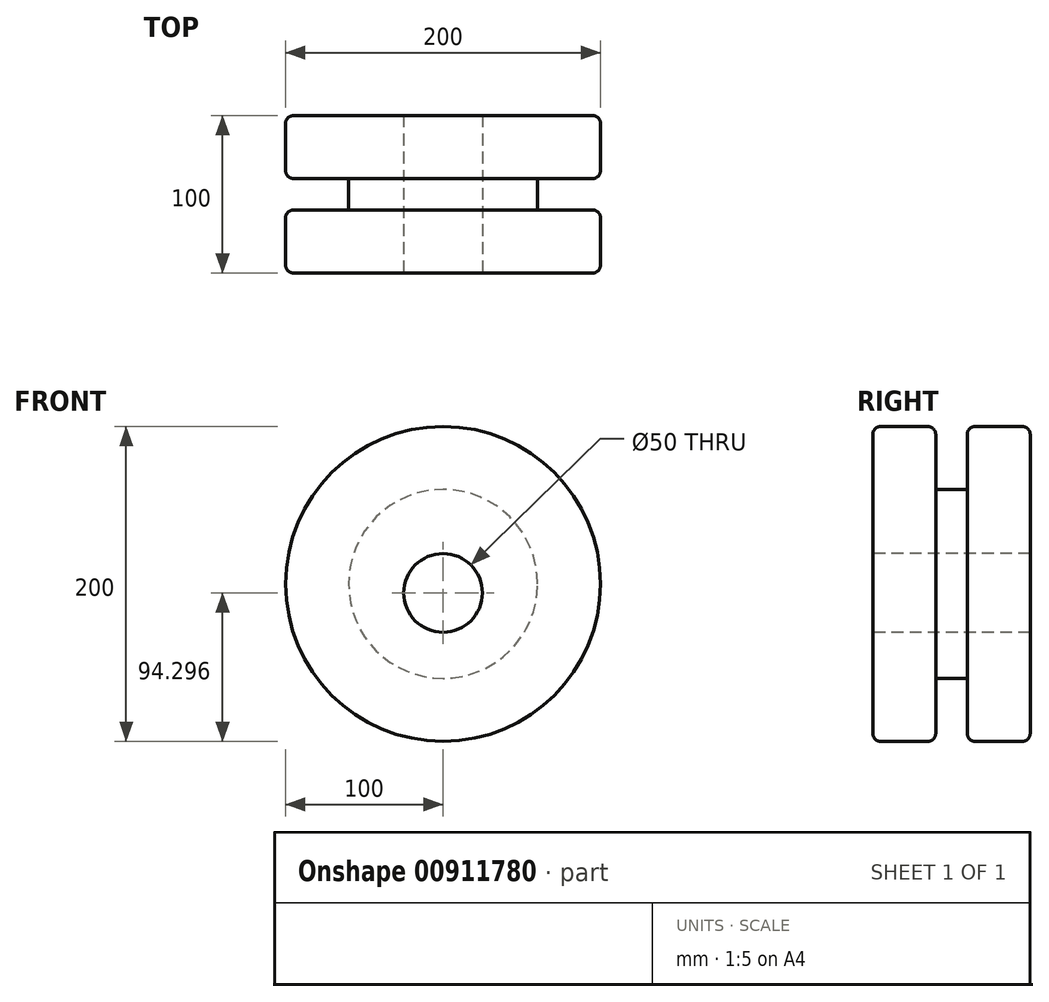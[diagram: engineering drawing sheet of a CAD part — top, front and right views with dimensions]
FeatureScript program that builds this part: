
annotation { "Feature Type Name" : "Feature", "Feature Type Description" : "" }
export const myFeature = defineFeature(function(context is Context, id is Id, definition is map)
    precondition{}
    {
        {
            var Q0;
            Q0=qCreatedBy(makeId("Front.planeOp"),FACE);
            var sketch = newSketch(context, id + "F0", { "sketchPlane" : qUnion([Q0])});
            skCircle(sketch, "E0", {"center": v(0, 0) * mm, "radius": 100 * mm});
            skSolve(sketch);
        }
        {
            var Q0;
            Q0=qSketchRegion(id+"F0",true);
            extrude(context, id + "F1", {"entities" : qUnion([Q0]), "depth" : 40 * mm, "offsetDistance" : 25 * mm});
        }
        {
            var Q0;
            Q0=makeQuery(id+"F1.opExtrude","CAP_FACE",FACE,{"disambiguationData":[OSD([sQuery(id+"F0.wireOp",EDGE,"E0")])],"isStart":false});
            var sketch = newSketch(context, id + "F2", { "sketchPlane" : qUnion([Q0])});
            skCircle(sketch, "E1", {"center": v(0, 0) * mm, "radius": 60 * mm});
            skSolve(sketch);
        }
        {
            var Q0;
            Q0=qSketchRegion(id+"F2",true);
            extrude(context, id + "F3", {"entities" : qUnion([Q0]), "operationType" : NewBodyOperationType.ADD, "depth" : 20 * mm, "offsetDistance" : 25 * mm});
        }
        {
            var Q0;
            Q0=makeQuery(id+"F3.opExtrude","CAP_FACE",FACE,{"disambiguationData":[OSD([sQuery(id+"F2.wireOp",EDGE,"E1")])],"isStart":false});
            var sketch = newSketch(context, id + "F4", { "sketchPlane" : qUnion([Q0])});
            skCircle(sketch, "E2", {"center": v(0, 0) * mm, "radius": 100 * mm});
            skSolve(sketch);
        }
        {
            var Q0;
            Q0=qSketchRegion(id+"F4",true);
            extrude(context, id + "F5", {"entities" : qUnion([Q0]), "operationType" : NewBodyOperationType.ADD, "depth" : 40 * mm, "offsetDistance" : 25 * mm});
        }
        {
            var Q0;
            Q0=makeQuery(id+"F5.opExtrude","CAP_FACE",FACE,{"disambiguationData":[OSD([sQuery(id+"F4.wireOp",EDGE,"E2")])],"isStart":false});
            var sketch = newSketch(context, id + "F6", { "sketchPlane" : qUnion([Q0])});
            skCircle(sketch, "E3", {"center": v(0, -5.7) * mm, "radius": 25 * mm});
            skSolve(sketch);
        }
        {
            var Q0;
            Q0=qSketchRegion(id+"F6",true);
            extrude(context, id + "F7", {"entities" : qUnion([Q0]), "operationType" : NewBodyOperationType.REMOVE, "oppositeDirection" : true, "depth" : 100 * mm, "offsetDistance" : 25 * mm});
        }
        {
            var Q0;
            Q0=makeQuery(id+"F5.opExtrude","CAP_EDGE",EDGE,{"disambiguationData":[OSD([sQuery(id+"F4.wireOp",EDGE,"E2")])],"isStart":false});
            var Q1;
            Q1=makeQuery(id+"F5.opExtrude","CAP_EDGE",EDGE,{"disambiguationData":[OSD([sQuery(id+"F4.wireOp",EDGE,"E2")])],"isStart":true});
            var Q2;
            Q2=makeQuery(id+"F1.opExtrude","CAP_EDGE",EDGE,{"disambiguationData":[OSD([sQuery(id+"F0.wireOp",EDGE,"E0")])],"isStart":false});
            var Q3;
            Q3=makeQuery(id+"F1.opExtrude","CAP_EDGE",EDGE,{"disambiguationData":[OSD([sQuery(id+"F0.wireOp",EDGE,"E0")])],"isStart":true});
            fillet(context, id + "F8", {"entities" : qUnion([Q0, Q1, Q2, Q3]), "radius" : 5 * mm, "tangentPropagation" : true, "allowEdgeOverflow" : false});
        }
    });
